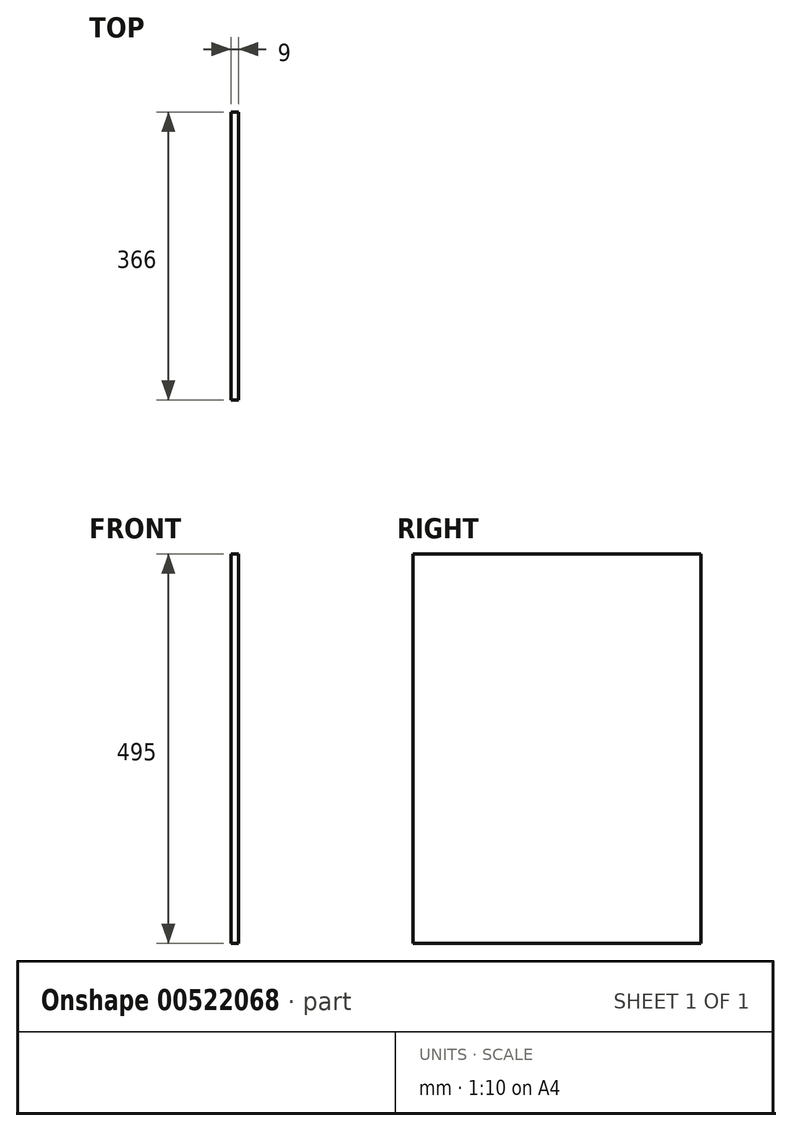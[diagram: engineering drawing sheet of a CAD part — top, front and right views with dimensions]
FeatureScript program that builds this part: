
annotation { "Feature Type Name" : "Feature", "Feature Type Description" : "" }
export const myFeature = defineFeature(function(context is Context, id is Id, definition is map)
    precondition{}
    {
        {
            var Q0;
            Q0=qCreatedBy(makeId("Right.planeOp"),FACE);
            var sketch = newSketch(context, id + "F0", { "sketchPlane" : qUnion([Q0])});
            skLineSegment(sketch, "E0", {"start": v(-366, 0) * mm, "end": v(-366, 495) * mm});
            skLineSegment(sketch, "E1", {"start": v(-366, 495) * mm, "end": v(0, 495) * mm});
            skLineSegment(sketch, "E2", {"start": v(0, 495) * mm, "end": v(0, 0) * mm});
            skLineSegment(sketch, "E3", {"start": v(0, 0) * mm, "end": v(-366, 0) * mm});
            skSolve(sketch);
        }
        {
            var Q0;
            Q0=makeQuery(id+"F0.imprint","IMPRINT",FACE,{"disambiguationData":[TD([[makeQuery(id+"F0.imprint","IMPRINT",EDGE,{"derivedFrom":sQuery(id+"F0.wireOp",EDGE,"E0")}),-1.0]])]});
            extrude(context, id + "F1", {"entities" : qUnion([Q0]), "depth" : 9 * mm, "offsetDistance" : 25 * mm});
        }
    });
